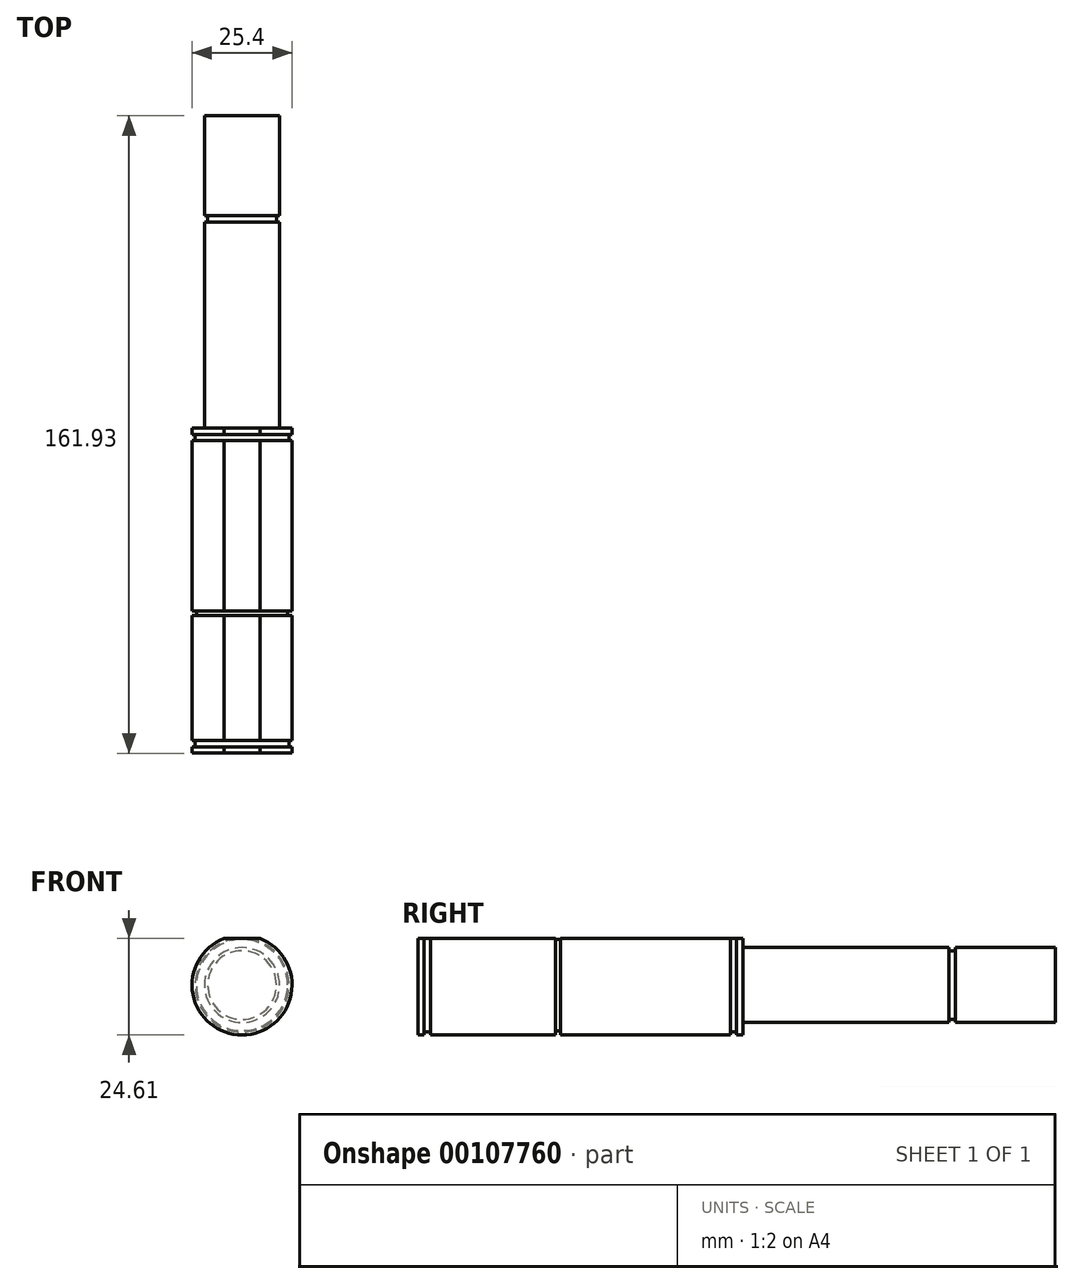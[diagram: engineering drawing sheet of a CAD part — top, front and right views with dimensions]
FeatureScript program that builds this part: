
annotation { "Feature Type Name" : "Feature", "Feature Type Description" : "" }
export const myFeature = defineFeature(function(context is Context, id is Id, definition is map)
    precondition{}
    {
        {
            var Q0;
            Q0=qCreatedBy(makeId("Front.planeOp"),FACE);
            var sketch = newSketch(context, id + "F0", { "sketchPlane" : qUnion([Q0])});
            skArc(sketch, "E0", {"start": v(-4.6, 11.84) * mm, "mid": v(0, -12.7) * mm, "end": v(4.6, 11.84) * mm});
            skLineSegment(sketch, "E1", {"start": v(-4.6, 11.84) * mm, "end": v(4.6, 11.84) * mm});
            skSolve(sketch);
        }
        {
            var Q0;
            Q0 = qSketchRegion(id + "F0", true);
            extrude(context, id + "F1", {"entities" : qUnion([Q0]), "depth" : 76.2 * mm});
        }
        {
            var Q0;
            Q0=makeQuery(id+"F1.opExtrude","CAP_FACE",FACE,{"disambiguationData":[OSD([sQuery(id+"F0.wireOp",EDGE,"E0")])],"isStart":false});
            var sketch = newSketch(context, id + "F2", { "sketchPlane" : qUnion([Q0])});
            skCircle(sketch, "E2", {"center": v(0, 0) * mm, "radius": 11.9 * mm});
            skSolve(sketch);
        }
        {
            var Q0;
            Q0 = qSketchRegion(id + "F2", true);
            extrude(context, id + "F3", {"entities" : qUnion([Q0]), "operationType" : NewBodyOperationType.ADD, "depth" : 1.59 * mm});
        }
        {
            var Q0;
            Q0=makeQuery(id+"F3.opExtrude","CAP_FACE",FACE,{"disambiguationData":[OSD([sQuery(id+"F2.wireOp",EDGE,"E2")])],"isStart":false});
            var sketch = newSketch(context, id + "F4", { "sketchPlane" : qUnion([Q0])});
            skArc(sketch, "E3", {"start": v(-4.61, 11.83) * mm, "mid": v(0, -12.7) * mm, "end": v(4.61, 11.83) * mm});
            skLineSegment(sketch, "E4", {"start": v(-4.61, 11.83) * mm, "end": v(4.61, 11.83) * mm});
            skSolve(sketch);
        }
        {
            var Q0;
            Q0 = qSketchRegion(id + "F4", true);
            extrude(context, id + "F5", {"entities" : qUnion([Q0]), "operationType" : NewBodyOperationType.ADD, "depth" : 1.59 * mm});
        }
        {
            var Q0;
            Q0=makeQuery(id+"F1.opExtrude","CAP_FACE",FACE,{"disambiguationData":[OSD([sQuery(id+"F0.wireOp",EDGE,"E0")])],"isStart":true});
            var sketch = newSketch(context, id + "F6", { "sketchPlane" : qUnion([Q0])});
            skCircle(sketch, "E5", {"center": v(0, 0) * mm, "radius": 11.9 * mm});
            skSolve(sketch);
        }
        {
            var Q0;
            Q0 = qSketchRegion(id + "F6", true);
            extrude(context, id + "F7", {"entities" : qUnion([Q0]), "operationType" : NewBodyOperationType.ADD, "depth" : 1.59 * mm});
        }
        {
            var Q0;
            Q0=makeQuery(id+"F7.opExtrude","CAP_FACE",FACE,{"disambiguationData":[OSD([sQuery(id+"F6.wireOp",EDGE,"E5")])],"isStart":false});
            var sketch = newSketch(context, id + "F8", { "sketchPlane" : qUnion([Q0])});
            skArc(sketch, "E6", {"start": v(-4.52, 11.87) * mm, "mid": v(0, -12.7) * mm, "end": v(4.52, 11.87) * mm});
            skLineSegment(sketch, "E7", {"start": v(-4.52, 11.87) * mm, "end": v(4.52, 11.87) * mm});
            skSolve(sketch);
        }
        {
            var Q0;
            Q0 = qSketchRegion(id + "F8", true);
            extrude(context, id + "F9", {"entities" : qUnion([Q0]), "operationType" : NewBodyOperationType.ADD, "depth" : 1.59 * mm});
        }
        {
            var Q0;
            Q0=makeQuery(id+"F9.opExtrude","CAP_FACE",FACE,{"disambiguationData":[OSD([sQuery(id+"F8.wireOp",EDGE,"E6")])],"isStart":false});
            var sketch = newSketch(context, id + "F10", { "sketchPlane" : qUnion([Q0])});
            skCircle(sketch, "E8", {"center": v(0, 0) * mm, "radius": 9.53 * mm});
            skSolve(sketch);
        }
        {
            var Q0;
            Q0 = qSketchRegion(id + "F10", true);
            extrude(context, id + "F11", {"entities" : qUnion([Q0]), "operationType" : NewBodyOperationType.ADD, "depth" : 52.4 * mm});
        }
        {
            var Q0;
            Q0=makeQuery(id+"F11.opExtrude","CAP_FACE",FACE,{"disambiguationData":[OSD([sQuery(id+"F10.wireOp",EDGE,"E8")])],"isStart":false});
            var sketch = newSketch(context, id + "F12", { "sketchPlane" : qUnion([Q0])});
            skCircle(sketch, "E9", {"center": v(0, 0) * mm, "radius": 8.73 * mm});
            skSolve(sketch);
        }
        {
            var Q0;
            Q0 = qSketchRegion(id + "F12", true);
            extrude(context, id + "F13", {"entities" : qUnion([Q0]), "operationType" : NewBodyOperationType.ADD, "depth" : 1.59 * mm});
        }
        {
            var Q0;
            Q0=makeQuery(id+"F13.opExtrude","CAP_FACE",FACE,{"disambiguationData":[OSD([sQuery(id+"F12.wireOp",EDGE,"E9")])],"isStart":false});
            var sketch = newSketch(context, id + "F14", { "sketchPlane" : qUnion([Q0])});
            skCircle(sketch, "E10", {"center": v(0, 0) * mm, "radius": 9.53 * mm});
            skSolve(sketch);
        }
        {
            var Q0;
            Q0 = qSketchRegion(id + "F14", true);
            extrude(context, id + "F15", {"entities" : qUnion([Q0]), "operationType" : NewBodyOperationType.ADD, "depth" : 25.4 * mm});
        }
        {
            var Q0;
            Q0=qCreatedBy(makeId("Right.planeOp"),FACE);
            var sketch = newSketch(context, id + "F16", { "sketchPlane" : qUnion([Q0])});
            skLineSegment(sketch, "E11", {"start": v(-76.16, -12.8) * mm, "end": v(-44.41, -12.8) * mm});
            skLineSegment(sketch, "E12.bottom", {"start": v(-44.41, -12.8) * mm, "end": v(-43.22, -12.8) * mm});
            skLineSegment(sketch, "E12.top", {"start": v(-44.41, -11.6) * mm, "end": v(-43.22, -11.6) * mm});
            skLineSegment(sketch, "E12.left", {"start": v(-44.41, -12.8) * mm, "end": v(-44.41, -11.6) * mm});
            skLineSegment(sketch, "E12.right", {"start": v(-43.22, -12.8) * mm, "end": v(-43.22, -11.6) * mm});
            skSolve(sketch);
        }
        {
            var Q0;
            Q0 = qSketchRegion(id + "F16", true);
            var Q1;
            Q1=makeQuery(id+"F1.opExtrude","SWEPT_FACE",FACE,{"disambiguationData":[OSD([sQuery(id+"F0.wireOp",EDGE,"E0")])]});
            revolve(context, id + "F17", {"operationType" : NewBodyOperationType.REMOVE, "entities" : qUnion([Q0]), "axis" : qUnion([Q1]), "revolveType" : RevolveType.FULL, "oppositeDirection" : true});
        }
    });
